# Revit family: Facade_60_Curtain_Wall_E11_Standard
name_source: partatom
category: Windows
revit_build: Autodesk Revit 2014 (Build: 20130308_1515(x64)
units: mm (PartAtom-declared; Revit-internal decimal feet)

## types (48) — shared parameters
100mm Mullion = Yes
160mm Mullion = No
190mm Mullion = No
DG Gasket Thickness = 12 mm  [stored 0.0393701 ft]
Description = Curtain wall, E11
Frame Bottom Gap = 30 mm  [stored 0.0984252 ft]
Frame Thickness = 102 mm
Glazing Bottom Gap = 70 mm
Glazing Side Gap = 40 mm  [stored 0.131234 ft]
Glazing Top Gap = 40 mm  [stored 0.131234 ft]
Half Expansion Break = No
Jamb Width = 60 mm  [stored 0.19685 ft]
Limit Door Height Max = 6110 mm
Limit Door Height Min = 410 mm
Limit Door Width Max = 3080 mm
Limit Door Width Min = 380 mm
Limit Panel Height Max = 6000 mm  [stored 19.685 ft]
Limit Panel Height Min = 300 mm
Limit Panel Width Max = 3000 mm  [stored 9.84252 ft]
Limit Panel Width Min = 300 mm
Manufacturer = Crealco
Max System DG Unit Thickness = 25 mm  [stored 0.082021 ft]
Model = Façade 60
Mullion Configuration = 1 mm  [stored 0.00328084 ft]
Sill Height = 85 mm  [stored 0.278871 ft]
Thermal Break Material = Plastic, Opaque Black
URL = http://www.crealco.co.za
Wall Closure = By host
zero-valued in all types: Custom Offset From Exterior, Default Sill Height

## per-type parameters (varying)
| type | Custom Curtain Wall Height | Custom Curtain Wall Width | Custom Windload | Intruderprufe Insulated LowE SHGC Value | Intruderprufe Insulated LowE U Value | Intruderprufe Insulated SHGC Value | Intruderprufe Insulated U Value | Intruderprufe LowE SHGC Value | Intruderprufe LowE U Value | Intruderprufe SHGC Value | Intruderprufe U Value | Quarter Expansion Break |
| F60-E11-0925-1000Pa | 2490 mm | 890 mm  [stored 2.91995 ft] | 1000 mm  [stored 3.28084 ft] | 0.515 | 2.64 | 0.571 | 3.24 | 0.581 | 4.39 | 0.662 | 5.75 | No |
| F60-E11-0925-1500Pa | 2490 mm | 890 mm  [stored 2.91995 ft] | 1500 mm  [stored 4.92126 ft] | 0.515 | 2.64 | 0.571 | 3.24 | 0.581 | 4.39 | 0.662 | 5.75 | No |
| F60-E11-0925-2000Pa | 2490 mm | 890 mm  [stored 2.91995 ft] | 2000 mm  [stored 6.56168 ft] | 0.515 | 2.64 | 0.571 | 3.24 | 0.581 | 4.39 | 0.662 | 5.75 | No |
| F60-E11-1225-1000Pa | 2490 mm | 1190 mm  [stored 3.9042 ft] | 1000 mm  [stored 3.28084 ft] | 5.34 | 0.52 | 0.592 | 3.15 | 0.602 | 4.27 | 0.687 | 5.76 | No |
| F60-E11-1225-1500Pa | 2490 mm | 1190 mm  [stored 3.9042 ft] | 1500 mm  [stored 4.92126 ft] | 5.34 | 0.52 | 0.592 | 3.15 | 0.602 | 4.27 | 0.687 | 5.76 | No |
| F60-E11-1225-2000Pa | 2490 mm | 1190 mm  [stored 3.9042 ft] | 2000 mm  [stored 6.56168 ft] | 5.34 | 0.52 | 0.592 | 3.15 | 0.602 | 4.27 | 0.687 | 5.76 | No |
| F60-E11-1525-1000Pa | 2490 mm | 1490 mm  [stored 4.88845 ft] | 1000 mm  [stored 3.28084 ft] | 0.544 | 2.45 | 0.604 | 3.1 | 0.615 | 4.19 | 0.701 | 5.76 | No |
| F60-E11-1525-1500Pa | 2490 mm | 1490 mm  [stored 4.88845 ft] | 1500 mm  [stored 4.92126 ft] | 0.544 | 2.45 | 0.604 | 3.1 | 0.615 | 4.19 | 0.701 | 5.76 | No |
| F60-E11-1525-2000Pa | 2490 mm | 1490 mm  [stored 4.88845 ft] | 2000 mm  [stored 6.56168 ft] | 0.544 | 2.45 | 0.604 | 3.1 | 0.615 | 4.19 | 0.701 | 5.76 | No |
| F60-E11-1825-1000Pa | 2490 mm | 1790 mm  [stored 5.8727 ft] | 1000 mm  [stored 3.28084 ft] | 0.552 | 2.4 | 0.612 | 3.07 | 0.623 | 4.15 | 0.711 | 5.76 | No |
| F60-E11-1825-1500Pa | 2490 mm | 1790 mm  [stored 5.8727 ft] | 1500 mm  [stored 4.92126 ft] | 0.552 | 2.4 | 0.612 | 3.07 | 0.623 | 4.15 | 0.711 | 5.76 | No |
| F60-E11-1825-2000Pa | 2490 mm | 1790 mm  [stored 5.8727 ft] | 2000 mm  [stored 6.56168 ft] | 0.552 | 2.4 | 0.612 | 3.07 | 0.623 | 4.15 | 0.711 | 5.76 | No |
| F60-E11-2125-1000Pa | 2490 mm | 2090 mm  [stored 6.85696 ft] | 1000 mm  [stored 3.28084 ft] | 0.557 | 2.37 | 0.618 | 3.04 | 0.629 | 4.11 | 0.718 | 5.77 | No |
| F60-E11-2125-1500Pa | 2490 mm | 2090 mm  [stored 6.85696 ft] | 1500 mm  [stored 4.92126 ft] | 0.557 | 2.37 | 0.618 | 3.04 | 0.629 | 4.11 | 0.718 | 5.77 | No |
| F60-E11-2125-2000Pa | 2490 mm | 2090 mm  [stored 6.85696 ft] | 2000 mm  [stored 6.56168 ft] | 0.557 | 2.37 | 0.618 | 3.04 | 0.629 | 4.11 | 0.718 | 5.77 | No |
| F60-E11-2425-1000Pa | 2490 mm | 2390 mm  [stored 7.84121 ft] | 1000 mm  [stored 3.28084 ft] | 0.561 | 2.34 | 0.622 | 3.03 | 0.633 | 4.08 | 0.723 | 5.77 | No |
| F60-E11-2425-1500Pa | 2490 mm | 2390 mm  [stored 7.84121 ft] | 1500 mm  [stored 4.92126 ft] | 0.561 | 2.34 | 0.622 | 3.03 | 0.633 | 4.08 | 0.723 | 5.77 | No |
| F60-E11-2425-2000Pa | 2490 mm | 2390 mm  [stored 7.84121 ft] | 2000 mm  [stored 6.56168 ft] | 0.561 | 2.34 | 0.622 | 3.03 | 0.633 | 4.08 | 0.723 | 5.77 | No |
| F60-E11-2725-1000Pa | 2490 mm | 2690 mm | 1000 mm  [stored 3.28084 ft] | 0.564 | 2.32 | 0.626 | 3.01 | 0.637 | 4.06 | 0.727 | 5.77 | No |
| F60-E11-2725-1500Pa | 2490 mm | 2690 mm | 1500 mm  [stored 4.92126 ft] | 0.564 | 2.32 | 0.626 | 3.01 | 0.637 | 4.06 | 0.727 | 5.77 | No |
| F60-E11-2725-2000Pa | 2490 mm | 2690 mm | 2000 mm  [stored 6.56168 ft] | 0.564 | 2.32 | 0.626 | 3.01 | 0.637 | 4.06 | 0.727 | 5.77 | No |
| F60-E11-3025-1000Pa | 2490 mm | 2990 mm  [stored 9.80971 ft] | 1000 mm  [stored 3.28084 ft] | 0.566 | 2.31 | 0.628 | 3 | 0.64 | 4.05 | 0.731 | 5.77 | No |
| F60-E11-3025-1500Pa | 2490 mm | 2990 mm  [stored 9.80971 ft] | 1500 mm  [stored 4.92126 ft] | 0.566 | 2.31 | 0.628 | 3 | 0.64 | 4.05 | 0.731 | 5.77 | No |
| F60-E11-3025-2000Pa | 2490 mm | 2990 mm  [stored 9.80971 ft] | 2000 mm  [stored 6.56168 ft] | 0.566 | 2.31 | 0.628 | 3 | 0.64 | 4.05 | 0.731 | 5.77 | No |
| F60-E11-0950-1000Pa | 4990 mm  [stored 16.3714 ft] | 890 mm  [stored 2.91995 ft] | 1000 mm  [stored 3.28084 ft] | 0.53 | 2.52 | 0.588 | 3.14 | 0.598 | 4.29 | 0.682 | 5.73 | No |
| F60-E11-0950-1500Pa | 4990 mm  [stored 16.3714 ft] | 890 mm  [stored 2.91995 ft] | 1500 mm  [stored 4.92126 ft] | 0.53 | 2.52 | 0.588 | 3.14 | 0.598 | 4.29 | 0.682 | 5.73 | No |
| F60-E11-0950-2000Pa | 4990 mm  [stored 16.3714 ft] | 890 mm  [stored 2.91995 ft] | 2000 mm  [stored 6.56168 ft] | 0.53 | 2.52 | 0.588 | 3.14 | 0.598 | 4.29 | 0.682 | 5.73 | No |
| F60-E11-1250-1000Pa | 4990 mm  [stored 16.3714 ft] | 1190 mm  [stored 3.9042 ft] | 1000 mm  [stored 3.28084 ft] | 0.549 | 2.39 | 0.609 | 3.08 | 0.62 | 4.16 | 0.708 | 5.74 | No |
| F60-E11-1250-1500Pa | 4990 mm  [stored 16.3714 ft] | 1190 mm  [stored 3.9042 ft] | 1500 mm  [stored 4.92126 ft] | 0.549 | 2.39 | 0.609 | 3.08 | 0.62 | 4.16 | 0.708 | 5.74 | No |
| F60-E11-1250-2000Pa | 4990 mm  [stored 16.3714 ft] | 1190 mm  [stored 3.9042 ft] | 2000 mm  [stored 6.56168 ft] | 0.549 | 2.39 | 0.609 | 3.08 | 0.62 | 4.16 | 0.708 | 5.74 | No |
| F60-E11-1550-1000Pa | 4990 mm  [stored 16.3714 ft] | 1490 mm  [stored 4.88845 ft] | 1000 mm  [stored 3.28084 ft] | 0.56 | 2.32 | 0.622 | 3 | 0.633 | 4.08 | 0.723 | 5.74 | No |
| F60-E11-1550-1500Pa | 4990 mm  [stored 16.3714 ft] | 1490 mm  [stored 4.88845 ft] | 1500 mm  [stored 4.92126 ft] | 0.56 | 2.32 | 0.622 | 3 | 0.633 | 4.08 | 0.723 | 5.74 | No |
| F60-E11-1550-2000Pa | 4990 mm  [stored 16.3714 ft] | 1490 mm  [stored 4.88845 ft] | 2000 mm  [stored 6.56168 ft] | 0.56 | 2.32 | 0.622 | 3 | 0.633 | 4.08 | 0.723 | 5.74 | No |
| F60-E11-1850-1000Pa | 4990 mm  [stored 16.3714 ft] | 1790 mm  [stored 5.8727 ft] | 1000 mm  [stored 3.28084 ft] | 0.568 | 2.27 | 0.63 | 2.96 | 0.642 | 4.02 | 0.733 | 5.75 | No |
| F60-E11-1850-1500Pa | 4990 mm  [stored 16.3714 ft] | 1790 mm  [stored 5.8727 ft] | 1500 mm  [stored 4.92126 ft] | 0.568 | 2.27 | 0.63 | 2.96 | 0.642 | 4.02 | 0.733 | 5.75 | No |
| F60-E11-1850-2000Pa | 4990 mm  [stored 16.3714 ft] | 1790 mm  [stored 5.8727 ft] | 2000 mm  [stored 6.56168 ft] | 0.568 | 2.27 | 0.63 | 2.96 | 0.642 | 4.02 | 0.733 | 5.75 | No |
| F60-E11-2150-1000Pa | 4990 mm  [stored 16.3714 ft] | 2090 mm  [stored 6.85696 ft] | 1000 mm  [stored 3.28084 ft] | 0.573 | 2.23 | 0.636 | 2.94 | 0.648 | 3.99 | 0.74 | 5.75 | No |
| F60-E11-2150-1500Pa | 4990 mm  [stored 16.3714 ft] | 2090 mm  [stored 6.85696 ft] | 1500 mm  [stored 4.92126 ft] | 0.573 | 2.23 | 0.636 | 2.94 | 0.648 | 3.99 | 0.74 | 5.75 | No |
| F60-E11-2150-2000Pa | 4990 mm  [stored 16.3714 ft] | 2090 mm  [stored 6.85696 ft] | 2000 mm  [stored 6.56168 ft] | 0.573 | 2.23 | 0.636 | 2.94 | 0.648 | 3.99 | 0.74 | 5.75 | No |
| F60-E11-2450-1000Pa | 4990 mm  [stored 16.3714 ft] | 2390 mm  [stored 7.84121 ft] | 1000 mm  [stored 3.28084 ft] | 0.577 | 2.21 | 0.641 | 2.92 | 0.653 | 3.96 | 0.745 | 5.75 | No |
| F60-E11-2450-1500Pa | 4990 mm  [stored 16.3714 ft] | 2390 mm  [stored 7.84121 ft] | 1500 mm  [stored 4.92126 ft] | 0.577 | 2.21 | 0.641 | 2.92 | 0.653 | 3.96 | 0.745 | 5.75 | No |
| F60-E11-2450-2000Pa | 4990 mm  [stored 16.3714 ft] | 2390 mm  [stored 7.84121 ft] | 2000 mm  [stored 6.56168 ft] | 0.577 | 2.21 | 0.641 | 2.92 | 0.653 | 3.96 | 0.745 | 5.75 | No |
| F60-E11-2750-1000Pa | 4990 mm  [stored 16.3714 ft] | 2690 mm | 1000 mm  [stored 3.28084 ft] | 0.58 | 2.19 | 0.644 | 2.9 | 0.656 | 3.94 | 0.75 | 5.75 | No |
| F60-E11-2750-1500Pa | 4990 mm  [stored 16.3714 ft] | 2690 mm | 1500 mm  [stored 4.92126 ft] | 0.58 | 2.19 | 0.644 | 2.9 | 0.656 | 3.94 | 0.75 | 5.75 | No |
| F60-E11-2750-2000Pa | 4990 mm  [stored 16.3714 ft] | 2690 mm | 2000 mm  [stored 6.56168 ft] | 0.58 | 2.19 | 0.644 | 2.9 | 0.656 | 3.94 | 0.75 | 5.75 | No |
| F60-E11-3050-1000Pa | 4990 mm  [stored 16.3714 ft] | 2990 mm  [stored 9.80971 ft] | 1000 mm  [stored 3.28084 ft] | 0.583 | 2.17 | 0.647 | 2.89 | 0.659 | 3.92 | 0.753 | 5.75 | No |
| F60-E11-3050-1500Pa | 4990 mm  [stored 16.3714 ft] | 2990 mm  [stored 9.80971 ft] | 1500 mm  [stored 4.92126 ft] | 0.583 | 2.17 | 0.647 | 2.89 | 0.659 | 3.92 | 0.753 | 5.75 | No |
| F60-E11-3050-2000Pa | 4990 mm  [stored 16.3714 ft] | 2990 mm  [stored 9.80971 ft] | 2000 mm  [stored 6.56168 ft] | 0.583 | 2.17 | 0.647 | 2.89 | 0.659 | 3.92 | 0.753 | 5.75 | Yes |

note: [stored X ft] marks values corroborated as IEEE doubles in the binary element streams (Revit-internal decimal feet)

## geometry (parser evidence)
native form markers: Sweep x15
no freeform markers — native parametric forms only
